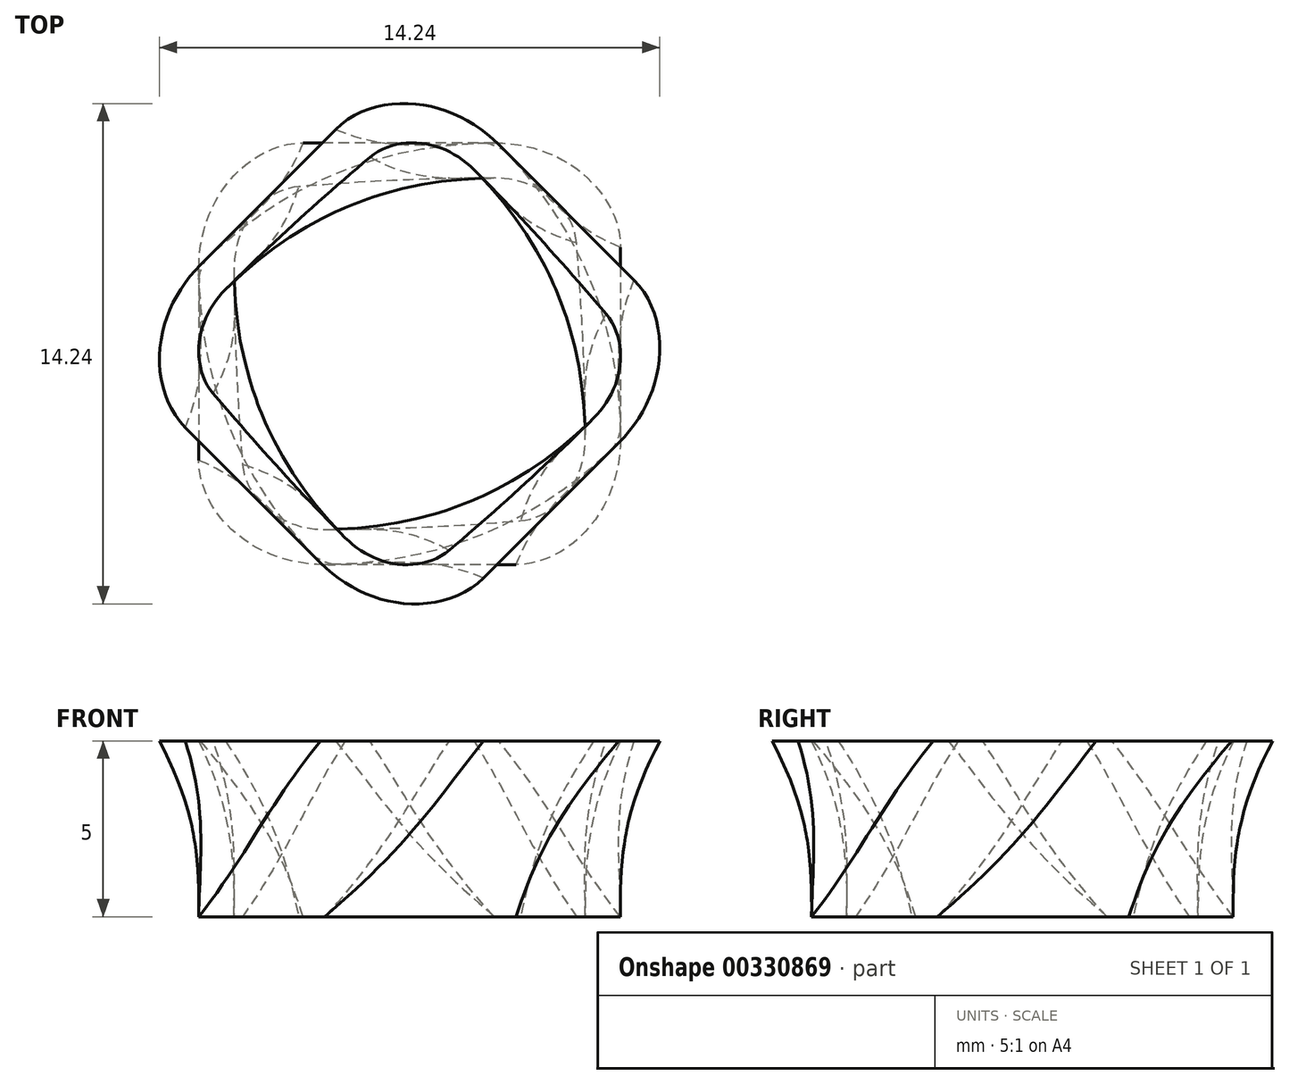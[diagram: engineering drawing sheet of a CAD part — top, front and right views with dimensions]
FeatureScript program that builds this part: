
annotation { "Feature Type Name" : "Feature", "Feature Type Description" : "" }
export const myFeature = defineFeature(function(context is Context, id is Id, definition is map)
    precondition{}
    {
        {
            var Q0;
            Q0=qCreatedBy(makeId("Top.planeOp"),FACE);
            var sketch = newSketch(context, id + "F0", { "sketchPlane" : qUnion([Q0])});
            skLineSegment(sketch, "E0.bottom", {"start": v(6, 6) * mm, "end": v(-6, 6) * mm});
            skLineSegment(sketch, "E0.top", {"start": v(6, -6) * mm, "end": v(-6, -6) * mm});
            skLineSegment(sketch, "E0.left", {"start": v(6, 6) * mm, "end": v(6, -6) * mm});
            skLineSegment(sketch, "E0.right", {"start": v(-6, 6) * mm, "end": v(-6, -6) * mm});
            skPoint(sketch, "E0.middle", {"position": v(0, 0) * mm});
            skSolve(sketch);
        }
        {
            var Q0;
            Q0=qCreatedBy(makeId("Top.planeOp"),FACE);
            cPlane(context, id + "F1", {"entities" : qUnion([Q0]), "cplaneType" : CPlaneType.OFFSET, "offset" : 5 * mm, "width" : 150 * mm, "height" : 150 * mm});
        }
        {
            var Q0;
            Q0=qCreatedBy(id+"F1.planeOp",FACE);
            var sketch = newSketch(context, id + "F2", { "sketchPlane" : qUnion([Q0])});
            skLineSegment(sketch, "E1.bottom", {"start": v(8.49, 0) * mm, "end": v(0, -8.49) * mm});
            skLineSegment(sketch, "E1.top", {"start": v(0, 8.49) * mm, "end": v(-8.49, 0) * mm});
            skLineSegment(sketch, "E1.left", {"start": v(8.49, 0) * mm, "end": v(0, 8.49) * mm});
            skLineSegment(sketch, "E1.right", {"start": v(0, -8.49) * mm, "end": v(-8.49, 0) * mm});
            skPoint(sketch, "E1.middle", {"position": v(0, 0) * mm});
            skSolve(sketch);
        }
        {
            var Q0;
            Q0=makeQuery(id+"F0.imprint","IMPRINT",FACE,{"disambiguationData":[TD([[makeQuery(id+"F0.imprint","IMPRINT",EDGE,{"derivedFrom":sQuery(id+"F0.wireOp",EDGE,"E0.bottom")}),1.0]])]});
            var Q1;
            Q1=makeQuery(id+"F2.imprint","IMPRINT",FACE,{"disambiguationData":[TD([[makeQuery(id+"F2.imprint","IMPRINT",EDGE,{"derivedFrom":sQuery(id+"F2.wireOp",EDGE,"E1.bottom")}),-1.0]])]});
            loft(context, id + "F3", {"sheetProfilesArray" : [{ "sheetProfileEntities" : qUnion([Q0]) }, { "sheetProfileEntities" : qUnion([Q1]) }]});
        }
        {
            var Q0;
            Q0=makeQuery(id+"F3.opLoft","CAP_FACE",FACE,{"disambiguationData":[OSD([makeQuery(id+"F2.imprint","IMPRINT",FACE,{"disambiguationData":[TD([[makeQuery(id+"F2.imprint","IMPRINT",EDGE,{"derivedFrom":sQuery(id+"F2.wireOp",EDGE,"E1.bottom")}),-1.0]])]})])],"isStart":true});
            var Q1;
            Q1=makeQuery(id+"F3.opLoft","CAP_FACE",FACE,{"disambiguationData":[OSD([makeQuery(id+"F0.imprint","IMPRINT",FACE,{"disambiguationData":[TD([[makeQuery(id+"F0.imprint","IMPRINT",EDGE,{"derivedFrom":sQuery(id+"F0.wireOp",EDGE,"E0.bottom")}),1.0]])]})])],"isStart":true});
            shell(context, id + "F4", {"entities" : qUnion([Q0, Q1]), "thickness" : 1 * mm});
        }
        {
            var Q0;
            Q0=makeQuery(id+"F4.opShell","OFFSET_EDGE",EDGE,{"disambiguationData":[OSD([sQuery(id+"F0.wireOp",EDGE,"E0.bottom"),sQuery(id+"F0.wireOp",EDGE,"E0.right"),sQuery(id+"F2.wireOp",EDGE,"E1.top"),sQuery(id+"F2.wireOp",EDGE,"E1.right")])]});
            var Q1;
            Q1=makeQuery(id+"F4.opShell","OFFSET_EDGE",EDGE,{"disambiguationData":[OSD([sQuery(id+"F0.wireOp",EDGE,"E0.top"),sQuery(id+"F0.wireOp",EDGE,"E0.right"),sQuery(id+"F2.wireOp",EDGE,"E1.bottom"),sQuery(id+"F2.wireOp",EDGE,"E1.right")])]});
            var Q2;
            Q2=makeQuery(id+"F4.opShell","OFFSET_EDGE",EDGE,{"disambiguationData":[OSD([sQuery(id+"F0.wireOp",EDGE,"E0.bottom"),sQuery(id+"F0.wireOp",EDGE,"E0.left"),sQuery(id+"F2.wireOp",EDGE,"E1.top"),sQuery(id+"F2.wireOp",EDGE,"E1.left")])]});
            var Q3;
            Q3=makeQuery(id+"F4.opShell","OFFSET_EDGE",EDGE,{"disambiguationData":[OSD([sQuery(id+"F0.wireOp",EDGE,"E0.top"),sQuery(id+"F0.wireOp",EDGE,"E0.left"),sQuery(id+"F2.wireOp",EDGE,"E1.bottom"),sQuery(id+"F2.wireOp",EDGE,"E1.left")])]});
            fillet(context, id + "F5", {"entities" : qUnion([Q0, Q1, Q2, Q3]), "radius" : 2 * mm, "tangentPropagation" : true, "allowEdgeOverflow" : false});
        }
        {
            var Q0;
            Q0=makeQuery(id+"F3.opLoft","SWEPT_EDGE",EDGE,{"disambiguationData":[OSD([sQuery(id+"F0.wireOp",EDGE,"E0.top"),sQuery(id+"F0.wireOp",EDGE,"E0.right"),sQuery(id+"F2.wireOp",EDGE,"E1.bottom"),sQuery(id+"F2.wireOp",EDGE,"E1.right")])]});
            var Q1;
            Q1=makeQuery(id+"F3.opLoft","SWEPT_EDGE",EDGE,{"disambiguationData":[OSD([sQuery(id+"F0.wireOp",EDGE,"E0.top"),sQuery(id+"F0.wireOp",EDGE,"E0.left"),sQuery(id+"F2.wireOp",EDGE,"E1.bottom"),sQuery(id+"F2.wireOp",EDGE,"E1.left")])]});
            var Q2;
            Q2=makeQuery(id+"F3.opLoft","SWEPT_EDGE",EDGE,{"disambiguationData":[OSD([sQuery(id+"F0.wireOp",EDGE,"E0.bottom"),sQuery(id+"F0.wireOp",EDGE,"E0.left"),sQuery(id+"F2.wireOp",EDGE,"E1.top"),sQuery(id+"F2.wireOp",EDGE,"E1.left")])]});
            var Q3;
            Q3=makeQuery(id+"F3.opLoft","SWEPT_EDGE",EDGE,{"disambiguationData":[OSD([sQuery(id+"F0.wireOp",EDGE,"E0.bottom"),sQuery(id+"F0.wireOp",EDGE,"E0.right"),sQuery(id+"F2.wireOp",EDGE,"E1.top"),sQuery(id+"F2.wireOp",EDGE,"E1.right")])]});
            fillet(context, id + "F6", {"entities" : qUnion([Q0, Q1, Q2, Q3]), "radius" : 3 * mm, "tangentPropagation" : true, "allowEdgeOverflow" : false});
        }
    });
